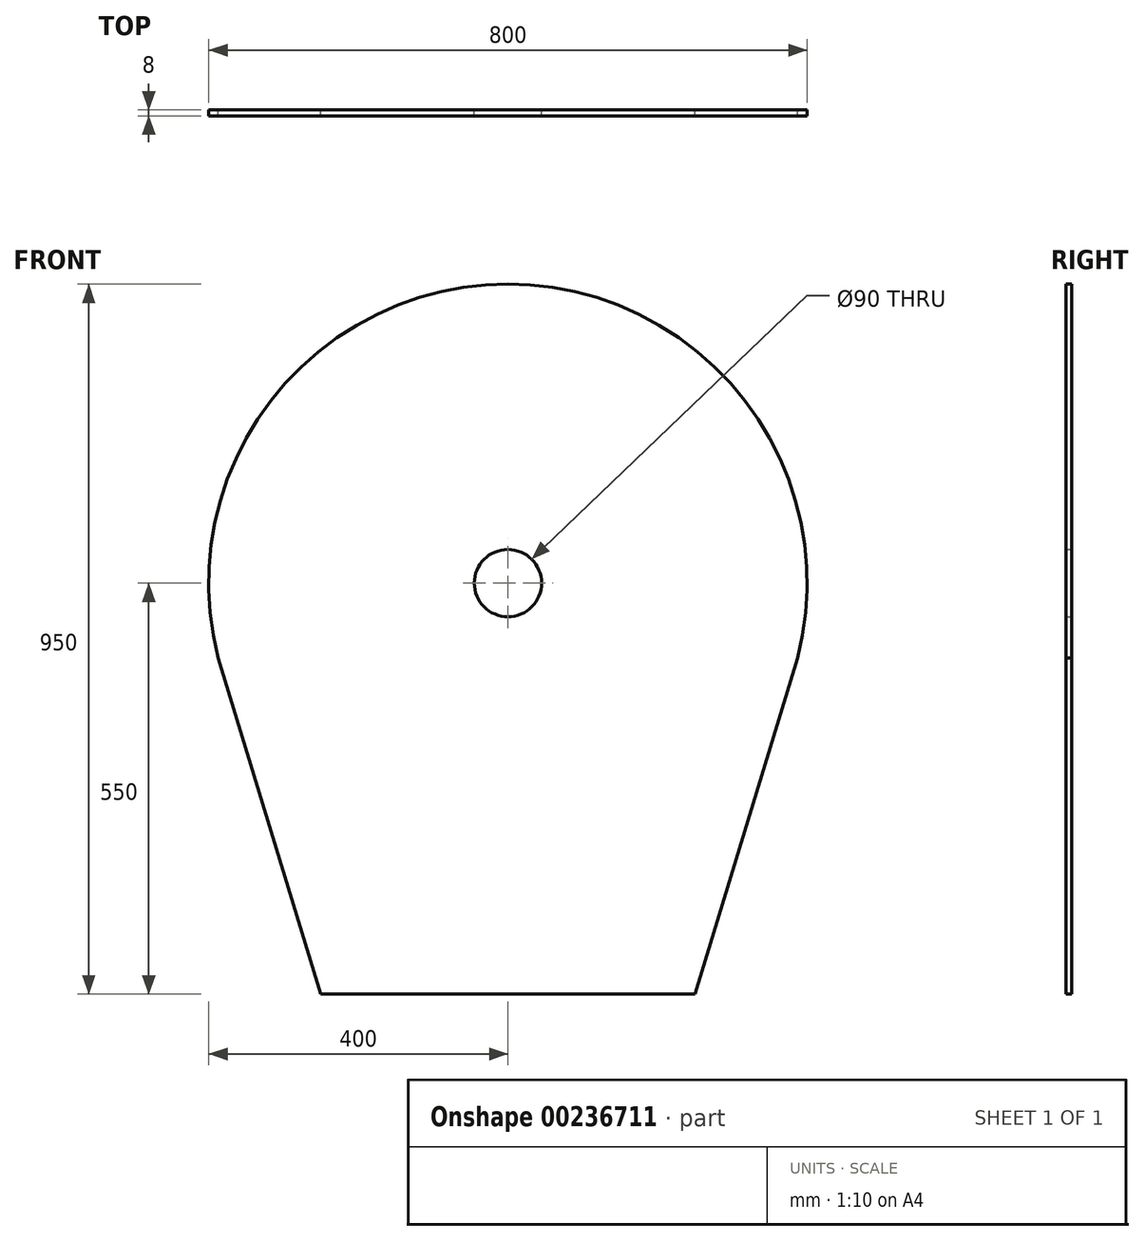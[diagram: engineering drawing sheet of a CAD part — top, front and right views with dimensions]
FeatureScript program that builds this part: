
annotation { "Feature Type Name" : "Feature", "Feature Type Description" : "" }
export const myFeature = defineFeature(function(context is Context, id is Id, definition is map)
    precondition{}
    {
        {
            var Q0;
            Q0=qCreatedBy(makeId("Front.planeOp"),FACE);
            var sketch = newSketch(context, id + "F0", { "sketchPlane" : qUnion([Q0])});
            skArc(sketch, "E0", {"start": v(387.3, -100) * mm, "mid": v(0, 400) * mm, "end": v(-387.3, -100) * mm});
            skLineSegment(sketch, "E1", {"start": v(24.55, -550) * mm, "end": v(250, -550) * mm});
            skLineSegment(sketch, "E2", {"start": v(250, -550) * mm, "end": v(387.3, -100) * mm});
            skLineSegment(sketch, "E3", {"start": v(-387.3, -100) * mm, "end": v(-250, -550) * mm});
            skLineSegment(sketch, "E4", {"start": v(-250, -550) * mm, "end": v(24.55, -550) * mm});
            skLineSegment(sketch, "E5", {"start": v(0, 400) * mm, "end": v(0, -605.38) * mm, "construction": true});
            skPoint(sketch, "E6.orphan", {"position": v(-387.3, -100) * mm});
            skCircle(sketch, "E7", {"center": v(0, 0) * mm, "radius": 45 * mm});
            skSolve(sketch);
        }
        {
            var Q0;
            Q0=makeQuery(id+"F0.imprint","IMPRINT",FACE,{"disambiguationData":[TD([[makeQuery(id+"F0.imprint","IMPRINT",EDGE,{"derivedFrom":sQuery(id+"F0.wireOp",EDGE,"E0")}),1.0]])]});
            extrude(context, id + "F1", {"entities" : qUnion([Q0]), "depth" : 8 * mm});
        }
    });
